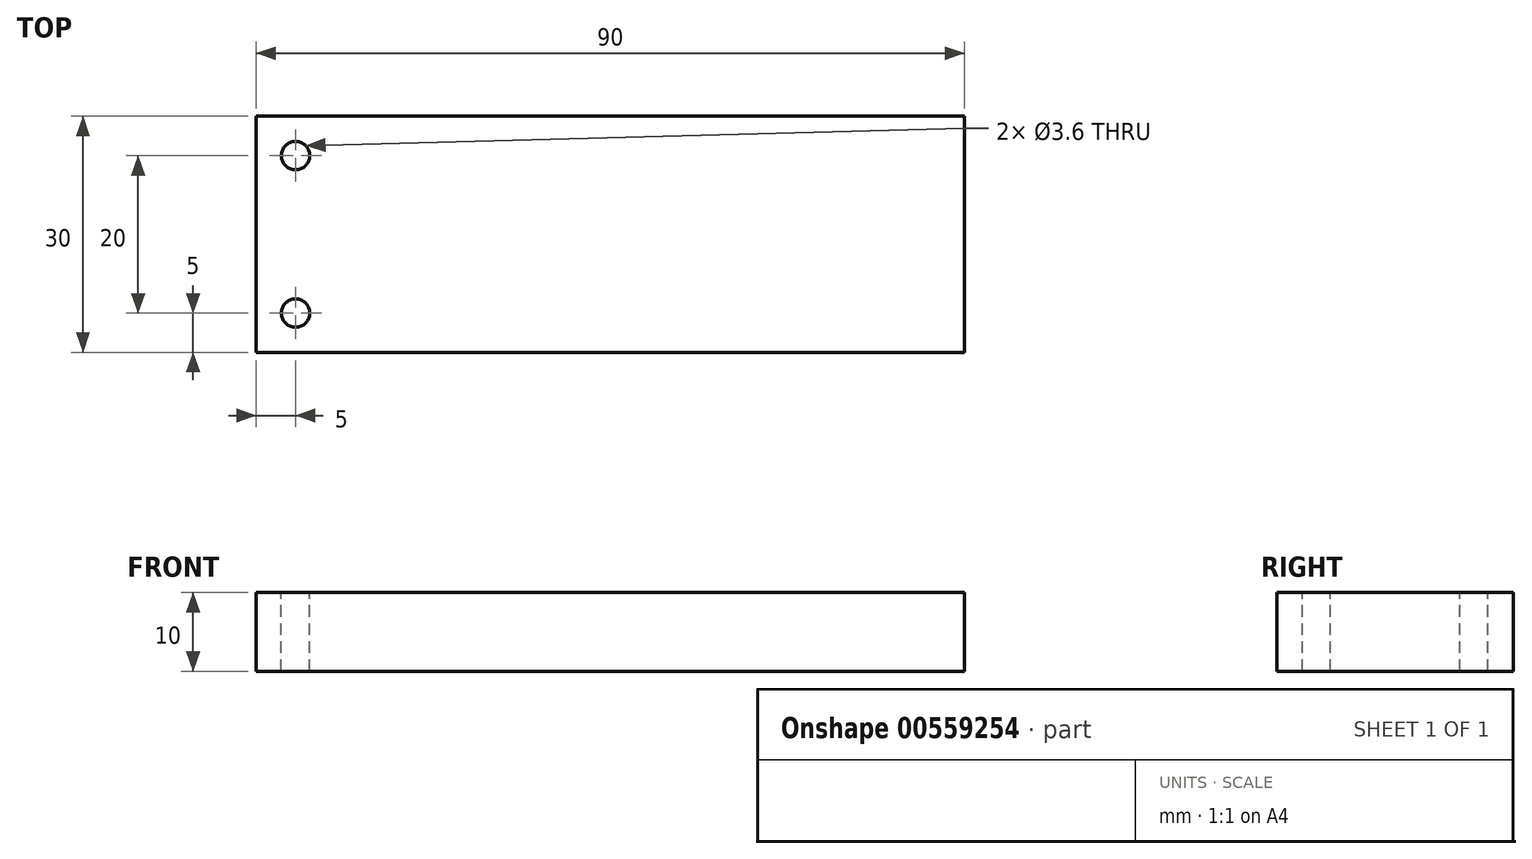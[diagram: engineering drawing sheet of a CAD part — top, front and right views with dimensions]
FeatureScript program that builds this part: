
annotation { "Feature Type Name" : "Feature", "Feature Type Description" : "" }
export const myFeature = defineFeature(function(context is Context, id is Id, definition is map)
    precondition{}
    {
        {
            var Q0;
            Q0=qCreatedBy(makeId("Top.planeOp"),FACE);
            var sketch = newSketch(context, id + "F0", { "sketchPlane" : qUnion([Q0])});
            skLineSegment(sketch, "E0.bottom", {"start": v(45, 15) * mm, "end": v(-45, 15) * mm});
            skLineSegment(sketch, "E0.top", {"start": v(45, -15) * mm, "end": v(-45, -15) * mm});
            skLineSegment(sketch, "E0.left", {"start": v(45, 15) * mm, "end": v(45, -15) * mm});
            skLineSegment(sketch, "E0.right", {"start": v(-45, 15) * mm, "end": v(-45, -15) * mm});
            skPoint(sketch, "E0.middle", {"position": v(0, 0) * mm});
            skSolve(sketch);
        }
        {
            var Q0;
            Q0 = qSketchRegion(id + "F0", true);
            extrude(context, id + "F1", {"entities" : qUnion([Q0]), "endBound" : BoundingType.SYMMETRIC, "depth" : 10 * mm, "offsetDistance" : 25 * mm});
        }
        {
            var Q0;
            Q0=makeQuery(id+"F1.opExtrude","CAP_FACE",FACE,{"disambiguationData":[OSD([sQuery(id+"F0.wireOp",EDGE,"E0.bottom"),sQuery(id+"F0.wireOp",EDGE,"E0.top"),sQuery(id+"F0.wireOp",EDGE,"E0.left"),sQuery(id+"F0.wireOp",EDGE,"E0.right")])],"isStart":false});
            var sketch = newSketch(context, id + "F2", { "sketchPlane" : qUnion([Q0])});
            skCircle(sketch, "E1", {"center": v(-40, 10) * mm, "radius": 1.8 * mm});
            skSolve(sketch);
        }
        {
            var Q0;
            Q0 = qSketchRegion(id + "F2", true);
            extrude(context, id + "F3", {"entities" : qUnion([Q0]), "operationType" : NewBodyOperationType.REMOVE, "oppositeDirection" : true, "depth" : 21 * mm, "offsetDistance" : 25 * mm});
        }
        {
            var Q0;
            Q0=makeQuery(id+"F1.opExtrude","CAP_FACE",FACE,{"disambiguationData":[OSD([sQuery(id+"F0.wireOp",EDGE,"E0.bottom"),sQuery(id+"F0.wireOp",EDGE,"E0.top"),sQuery(id+"F0.wireOp",EDGE,"E0.left"),sQuery(id+"F0.wireOp",EDGE,"E0.right")])],"isStart":false});
            var sketch = newSketch(context, id + "F4", { "sketchPlane" : qUnion([Q0])});
            skCircle(sketch, "E2", {"center": v(-40, -10) * mm, "radius": 1.8 * mm});
            skSolve(sketch);
        }
        {
            var Q0;
            Q0 = qSketchRegion(id + "F4", true);
            extrude(context, id + "F5", {"entities" : qUnion([Q0]), "operationType" : NewBodyOperationType.REMOVE, "oppositeDirection" : true, "depth" : 21 * mm, "offsetDistance" : 25 * mm});
        }
    });
